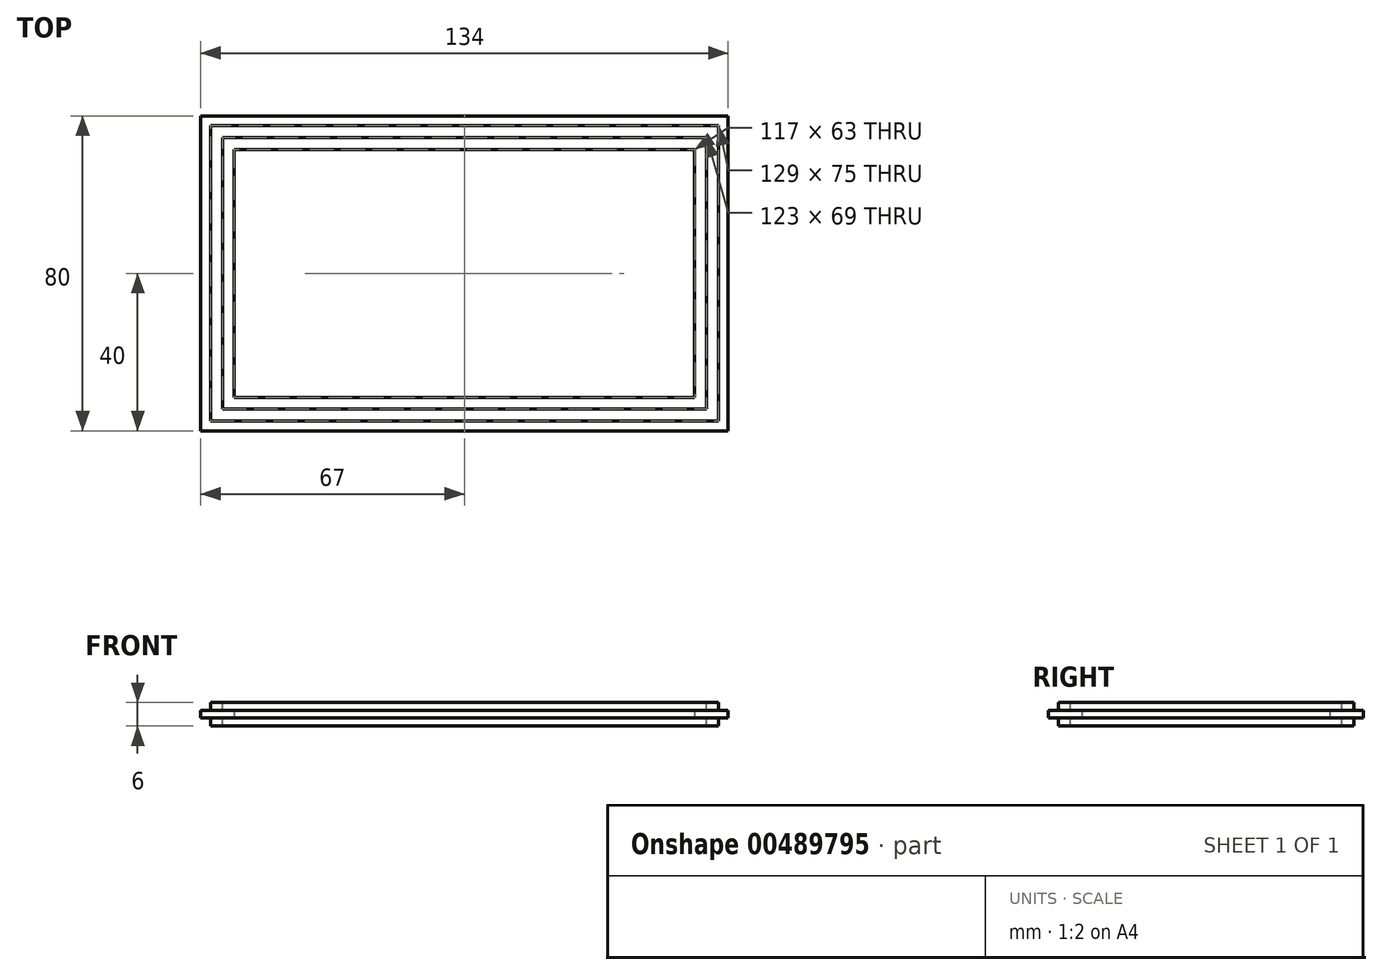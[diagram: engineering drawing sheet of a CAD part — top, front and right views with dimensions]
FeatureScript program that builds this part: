
annotation { "Feature Type Name" : "Feature", "Feature Type Description" : "" }
export const myFeature = defineFeature(function(context is Context, id is Id, definition is map)
    precondition{}
    {
        {
            var Q0;
            Q0=qCreatedBy(makeId("Top.planeOp"),FACE);
            var sketch = newSketch(context, id + "F0", { "sketchPlane" : qUnion([Q0])});
            skLineSegment(sketch, "E0.bottom", {"start": v(-67, 40) * mm, "end": v(67, 40) * mm});
            skLineSegment(sketch, "E0.top", {"start": v(-67, -40) * mm, "end": v(67, -40) * mm});
            skLineSegment(sketch, "E0.left", {"start": v(-67, 40) * mm, "end": v(-67, -40) * mm});
            skLineSegment(sketch, "E0.right", {"start": v(67, 40) * mm, "end": v(67, -40) * mm});
            skSolve(sketch);
        }
        {
            var Q0;
            Q0=makeQuery(id+"F0.imprint","IMPRINT",FACE,{"disambiguationData":[TD([[makeQuery(id+"F0.imprint","IMPRINT",EDGE,{"derivedFrom":sQuery(id+"F0.wireOp",EDGE,"E0.bottom")}),-1.0]])]});
            extrude(context, id + "F1", {"entities" : qUnion([Q0]), "depth" : 2 * mm});
        }
        {
            var Q0;
            Q0=makeQuery(id+"F1.opExtrude","CAP_FACE",FACE,{"disambiguationData":[OSD([sQuery(id+"F0.wireOp",EDGE,"E0.bottom"),sQuery(id+"F0.wireOp",EDGE,"E0.top"),sQuery(id+"F0.wireOp",EDGE,"E0.left"),sQuery(id+"F0.wireOp",EDGE,"E0.right")])],"isStart":true});
            var sketch = newSketch(context, id + "F2", { "sketchPlane" : qUnion([Q0])});
            skLineSegment(sketch, "E1.bottom", {"start": v(-64.5, 37.5) * mm, "end": v(64.5, 37.5) * mm});
            skLineSegment(sketch, "E1.top", {"start": v(-64.5, -37.5) * mm, "end": v(64.5, -37.5) * mm});
            skLineSegment(sketch, "E1.left", {"start": v(-64.5, 37.5) * mm, "end": v(-64.5, -37.5) * mm});
            skLineSegment(sketch, "E1.right", {"start": v(64.5, 37.5) * mm, "end": v(64.5, -37.5) * mm});
            skLineSegment(sketch, "E2.bottom", {"start": v(-61.5, 34.5) * mm, "end": v(61.5, 34.5) * mm});
            skLineSegment(sketch, "E2.top", {"start": v(-61.5, -34.5) * mm, "end": v(61.5, -34.5) * mm});
            skLineSegment(sketch, "E2.left", {"start": v(-61.5, 34.5) * mm, "end": v(-61.5, -34.5) * mm});
            skLineSegment(sketch, "E2.right", {"start": v(61.5, 34.5) * mm, "end": v(61.5, -34.5) * mm});
            skSolve(sketch);
        }
        {
            var Q0;
            Q0=makeQuery(id+"F2.imprint","IMPRINT",FACE,{"disambiguationData":[TD([[makeQuery(id+"F2.imprint","IMPRINT",EDGE,{"derivedFrom":sQuery(id+"F2.wireOp",EDGE,"E1.bottom")}),-1.0]])]});
            extrude(context, id + "F3", {"entities" : qUnion([Q0]), "operationType" : NewBodyOperationType.ADD, "depth" : 2 * mm, "hasSecondDirection" : true, "secondDirectionOppositeDirection" : true, "secondDirectionDepth" : 4 * mm});
        }
        {
            var Q0;
            Q0=makeQuery(id+"F3.boolean.opBoolean","SPLIT",FACE,{"disambiguationData":[TD([makeQuery(id+"F3.opExtrude","SWEPT_FACE",FACE,{"disambiguationData":[OSD([sQuery(id+"F2.wireOp",EDGE,"E2.bottom")])]})])],"derivedFrom":makeQuery(id+"F1.opExtrude","CAP_FACE",FACE,{"disambiguationData":[OSD([sQuery(id+"F0.wireOp",EDGE,"E0.bottom"),sQuery(id+"F0.wireOp",EDGE,"E0.top"),sQuery(id+"F0.wireOp",EDGE,"E0.left"),sQuery(id+"F0.wireOp",EDGE,"E0.right")])],"isStart":true})});
            var sketch = newSketch(context, id + "F4", { "sketchPlane" : qUnion([Q0])});
            skLineSegment(sketch, "E3.0.0", {"start": v(-61.5, 34.5) * mm, "end": v(-61.5, -34.5) * mm});
            skLineSegment(sketch, "E3.0.1", {"start": v(-61.5, -34.5) * mm, "end": v(61.5, -34.5) * mm});
            skLineSegment(sketch, "E3.0.2", {"start": v(61.5, -34.5) * mm, "end": v(61.5, 34.5) * mm});
            skLineSegment(sketch, "E3.0.3", {"start": v(61.5, 34.5) * mm, "end": v(-61.5, 34.5) * mm});
            skLineSegment(sketch, "E4.bottom", {"start": v(-58.5, 31.5) * mm, "end": v(58.5, 31.5) * mm});
            skLineSegment(sketch, "E4.top", {"start": v(-58.5, -31.5) * mm, "end": v(58.5, -31.5) * mm});
            skLineSegment(sketch, "E4.left", {"start": v(-58.5, 31.5) * mm, "end": v(-58.5, -31.5) * mm});
            skLineSegment(sketch, "E4.right", {"start": v(58.5, 31.5) * mm, "end": v(58.5, -31.5) * mm});
            skSolve(sketch);
        }
        {
            var Q0;
            Q0=makeQuery(id+"F4.imprint","IMPRINT",FACE,{"disambiguationData":[TD([[makeQuery(id+"F4.imprint","IMPRINT",EDGE,{"derivedFrom":sQuery(id+"F4.wireOp",EDGE,"E4.bottom")}),-1.0]])]});
            extrude(context, id + "F5", {"entities" : qUnion([Q0]), "operationType" : NewBodyOperationType.REMOVE, "oppositeDirection" : true, "depth" : 25 * mm});
        }
    });
